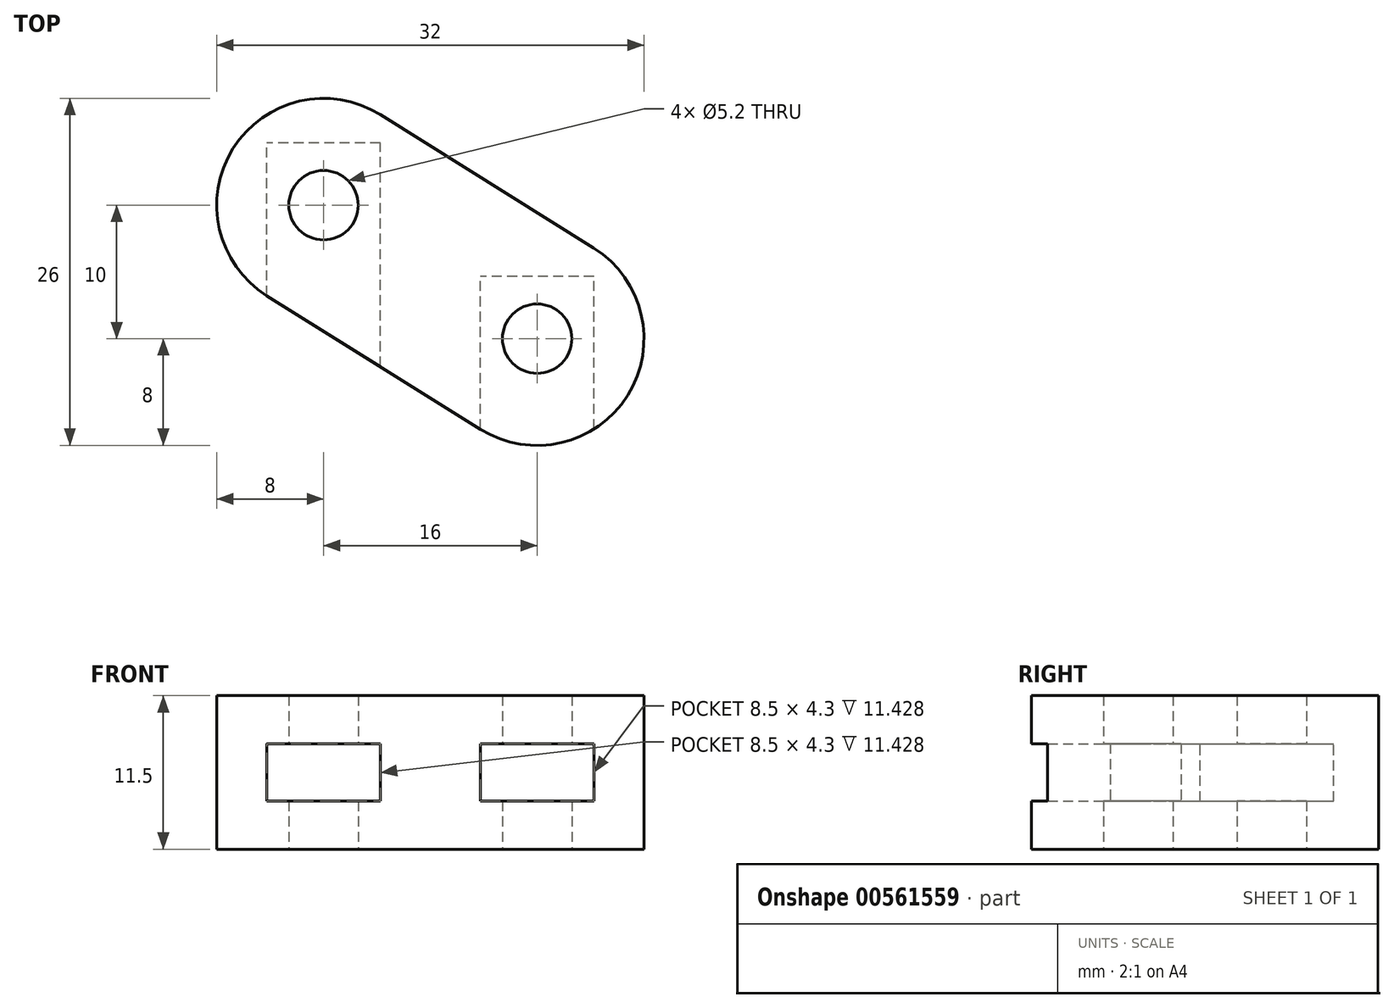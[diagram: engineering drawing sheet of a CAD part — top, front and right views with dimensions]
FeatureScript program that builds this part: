
annotation { "Feature Type Name" : "Feature", "Feature Type Description" : "" }
export const myFeature = defineFeature(function(context is Context, id is Id, definition is map)
    precondition{}
    {
        {
            var Q0;
            Q0=qCreatedBy(makeId("Top.planeOp"),FACE);
            var sketch = newSketch(context, id + "F0", { "sketchPlane" : qUnion([Q0])});
            skCircle(sketch, "E0", {"center": v(0, 0) * mm, "radius": 8 * mm});
            skCircle(sketch, "E1", {"center": v(16, -10) * mm, "radius": 8 * mm});
            skLineSegment(sketch, "E2", {"start": v(8, 0) * mm, "end": v(8, -10) * mm, "construction": true});
            skLineSegment(sketch, "E3", {"start": v(-4.24, -6.78) * mm, "end": v(11.76, -16.78) * mm});
            skLineSegment(sketch, "E4", {"start": v(4.24, 6.78) * mm, "end": v(20.24, -3.22) * mm});
            skCircle(sketch, "E5", {"center": v(0, 0) * mm, "radius": 2.6 * mm});
            skCircle(sketch, "E6", {"center": v(16, -10) * mm, "radius": 2.6 * mm});
            skSolve(sketch);
        }
        {
            var Q0;
            Q0=makeQuery(id+"F0.imprint","IMPRINT",FACE,{"disambiguationData":[TD([[makeQuery(id+"F0.imprint","IMPRINT",EDGE,{"derivedFrom":sQuery(id+"F0.wireOp",EDGE,"E5")}),-1.0]])]});
            var Q1;
            {var subQ0=sQuery(id+"F0.wireOp",EDGE,"E3");Q1=makeQuery(id+"F0.imprint","IMPRINT",FACE,{"disambiguationData":[TD([[makeQuery(id+"F0.imprint","IMPRINT",EDGE,{"derivedFrom":subQ0}),1.0]])]});}
            var Q2;
            Q2=makeQuery(id+"F0.imprint","IMPRINT",FACE,{"disambiguationData":[TD([[makeQuery(id+"F0.imprint","IMPRINT",EDGE,{"derivedFrom":sQuery(id+"F0.wireOp",EDGE,"E6")}),-1.0]])]});
            extrude(context, id + "F1", {"entities" : qUnion([Q0, Q1, Q2]), "depth" : 11.5 * mm});
        }
        {
            var Q0;
            Q0=makeQuery(id+"F1.opExtrude","CAP_FACE",FACE,{"disambiguationData":[OSD([sQuery(id+"F0.wireOp",EDGE,"E0"),sQuery(id+"F0.wireOp",EDGE,"E1"),sQuery(id+"F0.wireOp",EDGE,"E3"),sQuery(id+"F0.wireOp",EDGE,"E4"),sQuery(id+"F0.wireOp",EDGE,"E5"),sQuery(id+"F0.wireOp",EDGE,"E6")])],"isStart":false});
            var Q1;
            Q1=makeQuery(id+"F1.opExtrude","CAP_FACE",FACE,{"disambiguationData":[OSD([sQuery(id+"F0.wireOp",EDGE,"E0"),sQuery(id+"F0.wireOp",EDGE,"E1"),sQuery(id+"F0.wireOp",EDGE,"E3"),sQuery(id+"F0.wireOp",EDGE,"E4"),sQuery(id+"F0.wireOp",EDGE,"E5"),sQuery(id+"F0.wireOp",EDGE,"E6")])],"isStart":true});
            cPlane(context, id + "F2", {"entities" : qUnion([Q0, Q1]), "cplaneType" : CPlaneType.MID_PLANE, "offset" : 150 * mm, "width" : 150 * mm, "height" : 150 * mm});
        }
        {
            var Q0;
            Q0=qCreatedBy(id+"F2.planeOp",FACE);
            var sketch = newSketch(context, id + "F3", { "sketchPlane" : qUnion([Q0])});
            skLineSegment(sketch, "E7.rect.bottom", {"start": v(4.25, -4.65) * mm, "end": v(-4.25, -4.65) * mm});
            skLineSegment(sketch, "E7.rect.top", {"start": v(4.25, 4.65) * mm, "end": v(-4.25, 4.65) * mm});
            skLineSegment(sketch, "E7.rect.left", {"start": v(4.25, -4.65) * mm, "end": v(4.25, 4.65) * mm});
            skLineSegment(sketch, "E7.rect.right", {"start": v(-4.25, -4.65) * mm, "end": v(-4.25, 4.65) * mm});
            skPoint(sketch, "E7.rect.middle", {"position": v(0, 0) * mm});
            skLineSegment(sketch, "E8.bottom", {"start": v(-4.25, -4.65) * mm, "end": v(4.25, -4.65) * mm});
            skLineSegment(sketch, "E8.top", {"start": v(-4.25, -14.65) * mm, "end": v(4.25, -14.65) * mm});
            skLineSegment(sketch, "E8.left", {"start": v(-4.25, -4.65) * mm, "end": v(-4.25, -14.65) * mm});
            skLineSegment(sketch, "E8.right", {"start": v(4.25, -4.65) * mm, "end": v(4.25, -14.65) * mm});
            skLineSegment(sketch, "E9.rect.bottom", {"start": v(20.25, -14.65) * mm, "end": v(11.75, -14.65) * mm});
            skLineSegment(sketch, "E9.rect.top", {"start": v(20.25, -5.35) * mm, "end": v(11.75, -5.35) * mm});
            skLineSegment(sketch, "E9.rect.left", {"start": v(20.25, -14.65) * mm, "end": v(20.25, -5.35) * mm});
            skLineSegment(sketch, "E9.rect.right", {"start": v(11.75, -14.65) * mm, "end": v(11.75, -5.35) * mm});
            skPoint(sketch, "E9.rect.middle", {"position": v(16, -10) * mm});
            skLineSegment(sketch, "E10.bottom", {"start": v(11.75, -14.65) * mm, "end": v(20.25, -14.65) * mm});
            skLineSegment(sketch, "E10.top", {"start": v(11.75, -24.65) * mm, "end": v(20.25, -24.65) * mm});
            skLineSegment(sketch, "E10.left", {"start": v(11.75, -14.65) * mm, "end": v(11.75, -24.65) * mm});
            skLineSegment(sketch, "E10.right", {"start": v(20.25, -14.65) * mm, "end": v(20.25, -24.65) * mm});
            skSolve(sketch);
        }
        {
            var Q0;
            Q0=qSketchRegion(id+"F3",true);
            extrude(context, id + "F4", {"entities" : qUnion([Q0]), "operationType" : NewBodyOperationType.REMOVE, "endBound" : BoundingType.SYMMETRIC, "oppositeDirection" : true, "depth" : 4.3 * mm});
        }
    });
